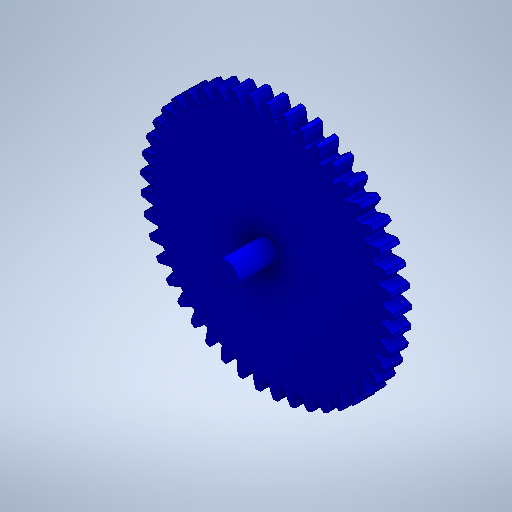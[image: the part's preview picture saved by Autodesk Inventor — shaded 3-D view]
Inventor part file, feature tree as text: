
AUTODESK INVENTOR PART (.ipt)
format: ipt  version: 2025.2 (Build 292293000, 293)  size: 480,256 bytes
history: native  units: mm (DEFAULTED — no unit token found)
features: plane x3, other x3, extrude x2, sketch x2
ambient origin geometry x8: Origin, YZ Plane, XZ Plane, XY Plane, X Axis, Y Axis, Z Axis, Center Point
bodies: Solid1 (feature_tree)
feature tree (10):
  extrude  "Extrusion1"  Depth=7.0mm TaperAngle=0.0deg
  plane  "Work Plane2"
  plane  "Work Plane8"
  plane  "Work Plane9"
  other  "Spur Gear"
  extrude  "Extrusion2"  Depth=10.0mm TaperAngle=0.0deg
  sketch  "Sketch1"  dims[d0=94.0mm d1=7.0mm d2=0.0mm]
  other  "Srf1"
  sketch  "Sketch3"  dims[d3=90.0mm d4=10.0mm d5=0.0mm d16=60.0mm d17=0.0mm d34=0.698132mm d39=0.0mm d41=0.0mm d43=60.0mm d46=60.0mm d47=0.0mm d48=0.0mm d49=8.0mm d50=15.0mm d51=0.0mm]
  other  "Pitch Diameter"
